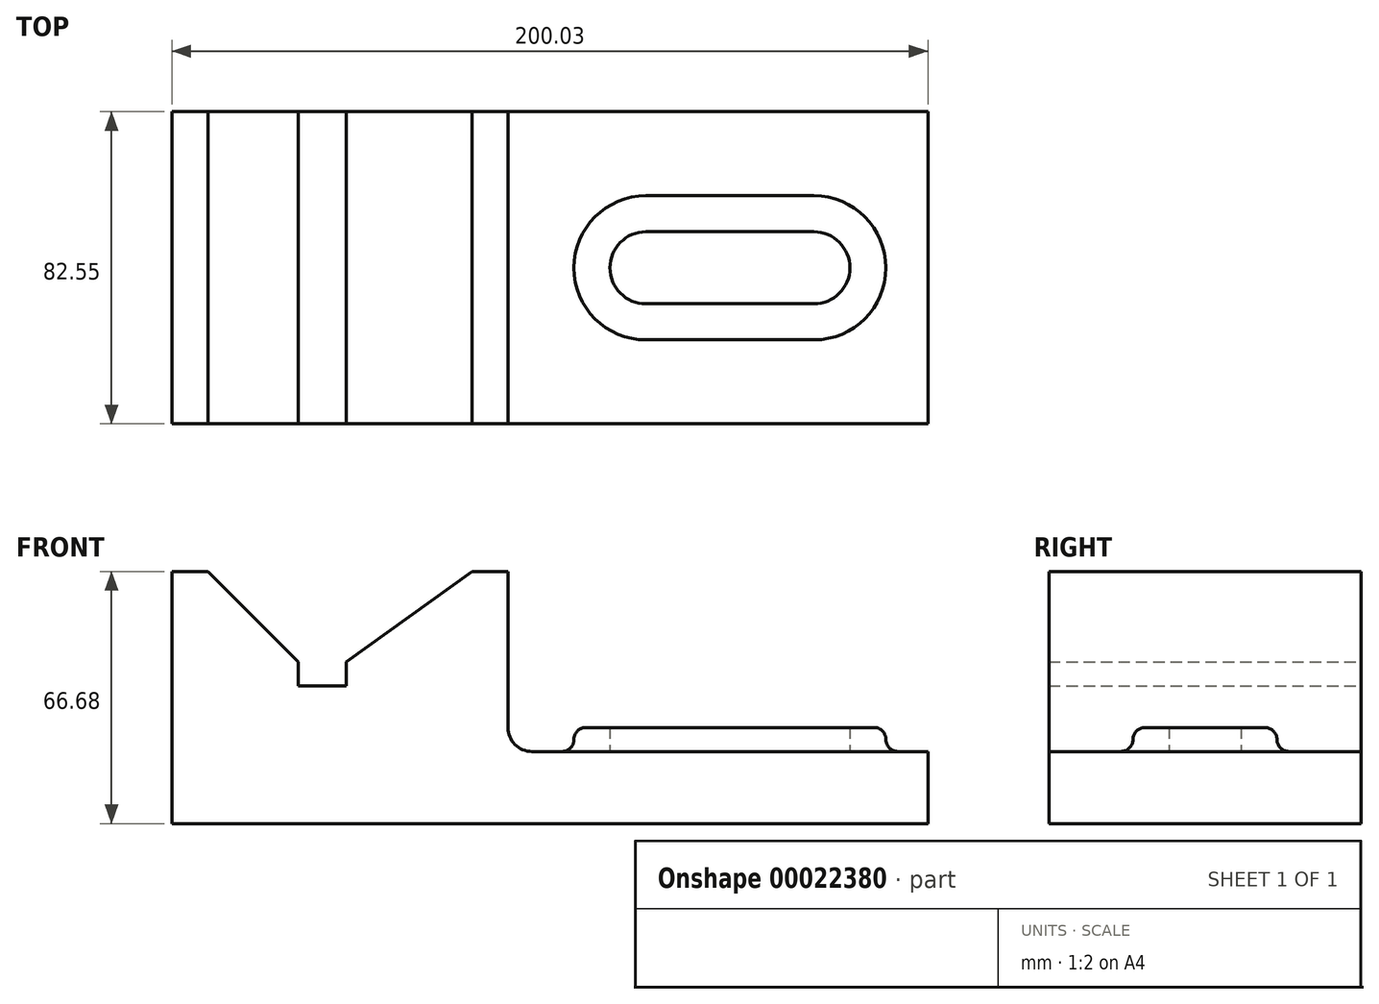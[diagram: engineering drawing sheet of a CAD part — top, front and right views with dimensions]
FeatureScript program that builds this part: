
annotation { "Feature Type Name" : "Feature", "Feature Type Description" : "" }
export const myFeature = defineFeature(function(context is Context, id is Id, definition is map)
    precondition{}
    {
        {
            var Q0;
            Q0=qCreatedBy(makeId("Front.planeOp"),FACE);
            var sketch = newSketch(context, id + "F0", { "sketchPlane" : qUnion([Q0])});
            skLineSegment(sketch, "E0.bottom", {"start": v(-148.79, 49.87) * mm, "end": v(51.24, 49.87) * mm});
            skLineSegment(sketch, "E0.top", {"start": v(-148.79, -16.8) * mm, "end": v(51.24, -16.8) * mm});
            skLineSegment(sketch, "E0.left", {"start": v(-148.79, 49.87) * mm, "end": v(-148.79, -16.8) * mm});
            skLineSegment(sketch, "E0.right", {"start": v(51.24, 49.87) * mm, "end": v(51.24, -16.8) * mm});
            skLineSegment(sketch, "E1", {"start": v(-148.79, 49.87) * mm, "end": v(-139.26, 49.87) * mm});
            skLineSegment(sketch, "E2", {"start": v(-139.26, 49.87) * mm, "end": v(-115.32, 25.92) * mm});
            skLineSegment(sketch, "E3", {"start": v(-115.32, 25.92) * mm, "end": v(-115.32, 19.57) * mm});
            skLineSegment(sketch, "E4", {"start": v(-115.32, 19.57) * mm, "end": v(-102.62, 19.57) * mm});
            skLineSegment(sketch, "E5", {"start": v(-102.62, 19.57) * mm, "end": v(-102.62, 25.92) * mm});
            skLineSegment(sketch, "E6", {"start": v(-115.32, 25.92) * mm, "end": v(-102.62, 25.92) * mm});
            skLineSegment(sketch, "E7", {"start": v(-102.62, 25.92) * mm, "end": v(-69.41, 49.87) * mm});
            skLineSegment(sketch, "E8", {"start": v(-69.41, 49.87) * mm, "end": v(-59.89, 49.87) * mm});
            skLineSegment(sketch, "E9", {"start": v(-139.26, 49.87) * mm, "end": v(-69.41, 49.87) * mm});
            skLineSegment(sketch, "E10", {"start": v(-59.89, 49.87) * mm, "end": v(-59.89, 8.6) * mm});
            skLineSegment(sketch, "E11", {"start": v(-53.54, 2.24) * mm, "end": v(51.24, 2.24) * mm});
            skPoint(sketch, "E12.visualSharp", {"position": v(-59.89, 2.24) * mm});
            skArc(sketch, "E12.filletArc", {"start": v(-59.89, 8.6) * mm, "mid": v(-58.03, 4.1) * mm, "end": v(-53.54, 2.24) * mm});
            skSolve(sketch);
        }
        {
            var Q0;
            {var subQ2=sQuery(id+"F0.wireOp",EDGE,"E0.top");Q0=makeQuery(id+"F0.imprint","IMPRINT",FACE,{"disambiguationData":[TD([[makeQuery(id+"F0.imprint","IMPRINT",EDGE,{"derivedFrom":subQ2}),1.0]])]});}
            extrude(context, id + "F1", {"entities" : qUnion([Q0]), "depth" : 82.55 * mm});
        }
        {
            var Q0;
            Q0=makeQuery(id+"F1.opExtrude","SWEPT_FACE",FACE,{"disambiguationData":[OSD([sQuery(id+"F0.wireOp",EDGE,"E11")])]});
            var sketch = newSketch(context, id + "F2", { "sketchPlane" : qUnion([Q0])});
            skLineSegment(sketch, "E13.rect.bottom", {"start": v(21.07, -22.23) * mm, "end": v(-23.38, -22.22) * mm});
            skLineSegment(sketch, "E13.rect.top", {"start": v(21.07, -60.33) * mm, "end": v(-23.38, -60.33) * mm});
            skLineSegment(sketch, "E13.rect.left", {"start": v(21.07, -22.23) * mm, "end": v(21.07, -60.33) * mm});
            skPoint(sketch, "E13.rect.middle", {"position": v(-1.15, -41.28) * mm});
            skLineSegment(sketch, "E14.rect.bottom", {"start": v(21.07, -31.75) * mm, "end": v(-23.38, -31.75) * mm});
            skLineSegment(sketch, "E14.rect.top", {"start": v(21.07, -50.8) * mm, "end": v(-23.38, -50.8) * mm});
            skLineSegment(sketch, "E14.rect.left", {"start": v(21.07, -31.75) * mm, "end": v(21.07, -50.8) * mm});
            skArc(sketch, "E15", {"start": v(-23.38, -22.22) * mm, "mid": v(-42.43, -41.27) * mm, "end": v(-23.38, -60.33) * mm});
            skArc(sketch, "E16", {"start": v(-23.38, -31.75) * mm, "mid": v(-32.9, -41.27) * mm, "end": v(-23.38, -50.8) * mm});
            skArc(sketch, "E17", {"start": v(21.07, -50.8) * mm, "mid": v(30.6, -41.28) * mm, "end": v(21.07, -31.75) * mm});
            skArc(sketch, "E18", {"start": v(21.07, -60.33) * mm, "mid": v(40.12, -41.28) * mm, "end": v(21.07, -22.23) * mm});
            skPoint(sketch, "E19.start.orphan", {"position": v(-53.54, -41.28) * mm});
            skPoint(sketch, "E20.start.orphan", {"position": v(-1.15, 0) * mm});
            skPoint(sketch, "E21.trimOffspring.end.orphan", {"position": v(-1.15, -82.55) * mm});
            skPoint(sketch, "E22.trimOffspring.end.orphan", {"position": v(51.24, -41.28) * mm});
            skSolve(sketch);
        }
        {
            var Q0;
            Q0 = qSketchRegion(id + "F2", true);
            extrude(context, id + "F3", {"entities" : qUnion([Q0]), "operationType" : NewBodyOperationType.ADD, "depth" : 6.35 * mm});
        }
        {
            var Q0;
            Q0=makeQuery(id+"F3.opExtrude","SWEPT_FACE",FACE,{"disambiguationData":[OSD([sQuery(id+"F2.wireOp",EDGE,"E18")])]});
            fillet(context, id + "F4", {"entities" : qUnion([Q0]), "radius" : 3.17 * mm, "tangentPropagation" : true, "allowEdgeOverflow" : false});
        }
    });
